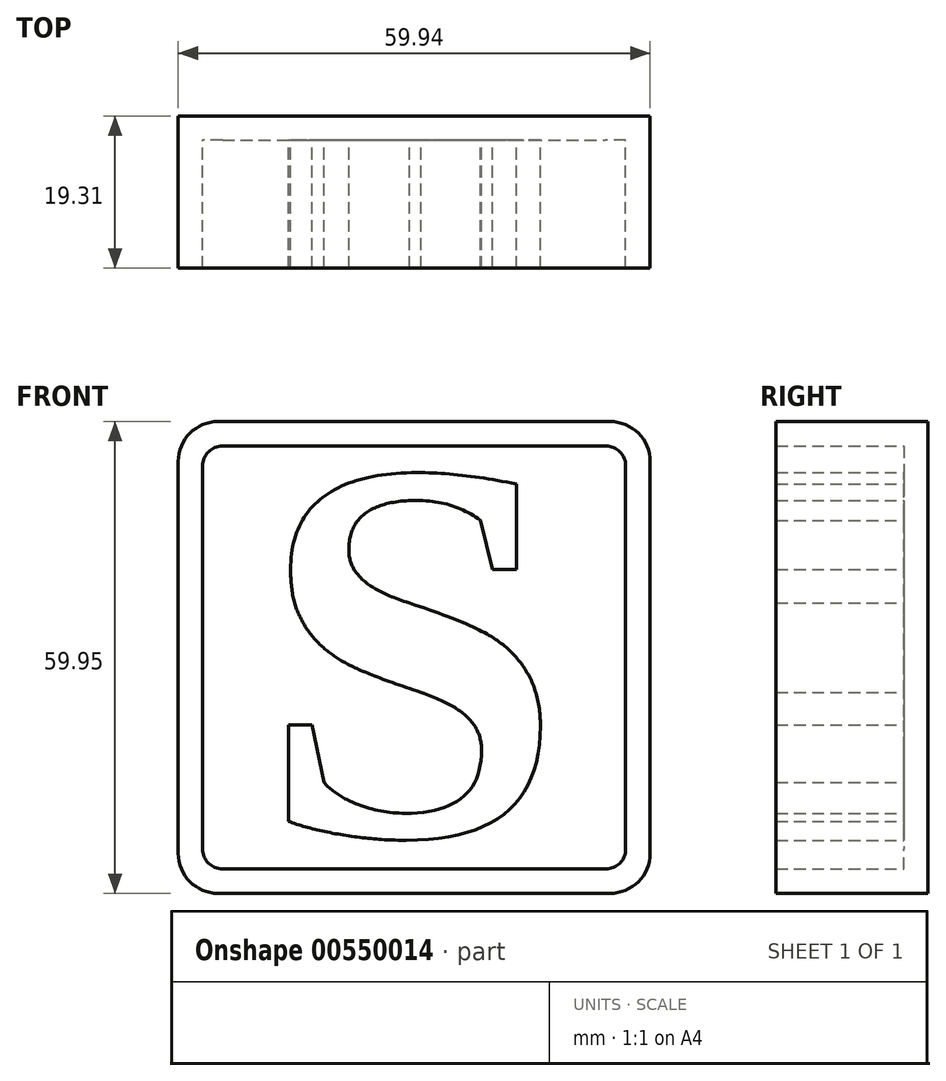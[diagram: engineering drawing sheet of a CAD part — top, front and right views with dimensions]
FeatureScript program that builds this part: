
annotation { "Feature Type Name" : "Feature", "Feature Type Description" : "" }
export const myFeature = defineFeature(function(context is Context, id is Id, definition is map)
    precondition{}
    {
        {
            var Q0;
            Q0=qCreatedBy(makeId("Front.planeOp"),FACE);
            var sketch = newSketch(context, id + "F0", { "sketchPlane" : qUnion([Q0])});
            skText(sketch, "E0", { "text": "S", "fontName": "Tinos-Bold.ttf"});
            const initialGuessF0  = {"E0": [-0.03634, -0.01847, 1, 0, 0.05004]};
            skSetInitialGuess(sketch, initialGuessF0);
            skSolve(sketch);
        }
        {
            var Q0;
            Q0=makeQuery(id+"F0.imprint","IMPRINT",FACE,{"disambiguationData":[TD([[makeQuery(id+"F0.imprint","IMPRINT",EDGE,{"derivedFrom":sQuery(id+"F0.wireOp",EDGE,"E0.sketch_text.stroke-0")}),-1.0]])]});
            extrude(context, id + "F1", {"entities" : qUnion([Q0]), "depth" : 9.9 * mm, "offsetDistance" : 25.4 * mm});
        }
        {
            var Q0;
            Q0=makeQuery(id+"F1.opExtrude","CAP_FACE",FACE,{"disambiguationData":[OSD([sQuery(id+"F0.wireOp",EDGE,"E0.sketch_text.stroke-0"),sQuery(id+"F0.wireOp",EDGE,"E0.sketch_text.stroke-1"),sQuery(id+"F0.wireOp",EDGE,"E0.sketch_text.stroke-2"),sQuery(id+"F0.wireOp",EDGE,"E0.sketch_text.stroke-3"),sQuery(id+"F0.wireOp",EDGE,"E0.sketch_text.stroke-4"),sQuery(id+"F0.wireOp",EDGE,"E0.sketch_text.stroke-5"),sQuery(id+"F0.wireOp",EDGE,"E0.sketch_text.stroke-6"),sQuery(id+"F0.wireOp",EDGE,"E0.sketch_text.stroke-7"),sQuery(id+"F0.wireOp",EDGE,"E0.sketch_text.stroke-8"),sQuery(id+"F0.wireOp",EDGE,"E0.sketch_text.stroke-9"),sQuery(id+"F0.wireOp",EDGE,"E0.sketch_text.stroke-10"),sQuery(id+"F0.wireOp",EDGE,"E0.sketch_text.stroke-11"),sQuery(id+"F0.wireOp",EDGE,"E0.sketch_text.stroke-12"),sQuery(id+"F0.wireOp",EDGE,"E0.sketch_text.stroke-13"),sQuery(id+"F0.wireOp",EDGE,"E0.sketch_text.stroke-14"),sQuery(id+"F0.wireOp",EDGE,"E0.sketch_text.stroke-15"),sQuery(id+"F0.wireOp",EDGE,"E0.sketch_text.stroke-16"),sQuery(id+"F0.wireOp",EDGE,"E0.sketch_text.stroke-17"),sQuery(id+"F0.wireOp",EDGE,"E0.sketch_text.stroke-18"),sQuery(id+"F0.wireOp",EDGE,"E0.sketch_text.stroke-19"),sQuery(id+"F0.wireOp",EDGE,"E0.sketch_text.stroke-20"),sQuery(id+"F0.wireOp",EDGE,"E0.sketch_text.stroke-21"),sQuery(id+"F0.wireOp",EDGE,"E0.sketch_text.stroke-22"),sQuery(id+"F0.wireOp",EDGE,"E0.sketch_text.stroke-23"),sQuery(id+"F0.wireOp",EDGE,"E0.sketch_text.stroke-24"),sQuery(id+"F0.wireOp",EDGE,"E0.sketch_text.stroke-25"),sQuery(id+"F0.wireOp",EDGE,"E0.sketch_text.stroke-26"),sQuery(id+"F0.wireOp",EDGE,"E0.sketch_text.stroke-27"),sQuery(id+"F0.wireOp",EDGE,"E0.sketch_text.stroke-28")])],"isStart":true});
            var sketch = newSketch(context, id + "F2", { "sketchPlane" : qUnion([Q0])});
            skLineSegment(sketch, "E1.bottom", {"start": v(-13.3, 34.04) * mm, "end": v(46.64, 34.04) * mm});
            skLineSegment(sketch, "E1.top", {"start": v(-13.3, -25.9) * mm, "end": v(46.64, -25.9) * mm});
            skLineSegment(sketch, "E1.left", {"start": v(-13.3, 34.04) * mm, "end": v(-13.3, -25.9) * mm});
            skLineSegment(sketch, "E1.right", {"start": v(46.64, 34.04) * mm, "end": v(46.64, -25.9) * mm});
            skSolve(sketch);
        }
        {
            var Q0;
            Q0=makeQuery(id+"F2.imprint","IMPRINT",FACE,{"disambiguationData":[TD([[makeQuery(id+"F2.imprint","IMPRINT",EDGE,{"derivedFrom":sQuery(id+"F2.wireOp",EDGE,"E1.bottom")}),-1.0]])]});
            var Q1;
            Q1=makeQuery(id+"F2.imprint","IMPRINT",FACE,{"disambiguationData":[TD([[makeQuery(id+"F2.imprint","IMPRINT",EDGE,{"derivedFrom":makeQuery(id+"F1.opExtrude","CAP_EDGE",EDGE,{"disambiguationData":[OSD([sQuery(id+"F0.wireOp",EDGE,"E0.sketch_text.stroke-0")])],"isStart":true})}),1.0]])]});
            var Q2;
            Q2=sQuery(id+"F2.wireOp",EDGE,"E1.right");
            var Q3;
            Q3=sQuery(id+"F2.wireOp",EDGE,"E1.bottom");
            var Q4;
            Q4=sQuery(id+"F2.wireOp",EDGE,"E1.top");
            var Q5;
            Q5=sQuery(id+"F2.wireOp",EDGE,"E1.left");
            extrude(context, id + "F3", {"entities" : qUnion([Q0, Q1]), "operationType" : NewBodyOperationType.ADD, "surfaceEntities" : qUnion([Q2, Q3, Q4, Q5]), "depth" : 3.05 * mm, "offsetDistance" : 25.4 * mm});
        }
        {
            var Q0;
            Q0=makeQuery(id+"F3.opExtrude","CAP_FACE",FACE,{"disambiguationData":[OSD([sQuery(id+"F2.wireOp",EDGE,"E1.bottom"),sQuery(id+"F2.wireOp",EDGE,"E1.top"),sQuery(id+"F2.wireOp",EDGE,"E1.left"),sQuery(id+"F2.wireOp",EDGE,"E1.right")])],"isStart":true});
            var sketch = newSketch(context, id + "F4", { "sketchPlane" : qUnion([Q0])});
            skLineSegment(sketch, "E2.bottom", {"start": v(-43.54, 30.94) * mm, "end": v(10.2, 30.94) * mm});
            skLineSegment(sketch, "E2.top", {"start": v(-43.54, -22.8) * mm, "end": v(10.2, -22.8) * mm});
            skLineSegment(sketch, "E2.left", {"start": v(-43.54, 30.94) * mm, "end": v(-43.54, -22.8) * mm});
            skLineSegment(sketch, "E2.right", {"start": v(10.2, 30.94) * mm, "end": v(10.2, -22.8) * mm});
            skSolve(sketch);
        }
        {
            var Q0;
            Q0=makeQuery(id+"F4.imprint","IMPRINT",FACE,{"disambiguationData":[TD([[makeQuery(id+"F4.imprint","IMPRINT",EDGE,{"derivedFrom":sQuery(id+"F4.wireOp",EDGE,"E2.bottom")}),1.0]])]});
            extrude(context, id + "F5", {"entities" : qUnion([Q0]), "operationType" : NewBodyOperationType.ADD, "depth" : 9.9 * mm, "offsetDistance" : 25.4 * mm});
        }
        {
            var Q0;
            {var subQ0=sQuery(id+"F2.wireOp",EDGE,"E1.left");var subQ1=sQuery(id+"F2.wireOp",EDGE,"E1.bottom");Q0=makeQuery(id+"F5.boolean.opBoolean","MERGE",EDGE,{"derivedFrom":[makeQuery(id+"F3.opExtrude","SWEPT_EDGE",EDGE,{"disambiguationData":[OSD([subQ1,subQ0])]}),makeQuery(id+"F5.opExtrude","SWEPT_EDGE",EDGE,{"disambiguationData":[OSD([subQ1,subQ0])]})]});}
            var Q1;
            {var subQ0=sQuery(id+"F2.wireOp",EDGE,"E1.right");var subQ1=sQuery(id+"F2.wireOp",EDGE,"E1.bottom");Q1=makeQuery(id+"F5.boolean.opBoolean","MERGE",EDGE,{"derivedFrom":[makeQuery(id+"F3.opExtrude","SWEPT_EDGE",EDGE,{"disambiguationData":[OSD([subQ1,subQ0])]}),makeQuery(id+"F5.opExtrude","SWEPT_EDGE",EDGE,{"disambiguationData":[OSD([subQ1,subQ0])]})]});}
            var Q2;
            {var subQ0=sQuery(id+"F2.wireOp",EDGE,"E1.right");var subQ1=sQuery(id+"F2.wireOp",EDGE,"E1.top");Q2=makeQuery(id+"F5.boolean.opBoolean","MERGE",EDGE,{"derivedFrom":[makeQuery(id+"F3.opExtrude","SWEPT_EDGE",EDGE,{"disambiguationData":[OSD([subQ1,subQ0])]}),makeQuery(id+"F5.opExtrude","SWEPT_EDGE",EDGE,{"disambiguationData":[OSD([subQ1,subQ0])]})]});}
            var Q3;
            {var subQ0=sQuery(id+"F2.wireOp",EDGE,"E1.left");var subQ1=sQuery(id+"F2.wireOp",EDGE,"E1.top");Q3=makeQuery(id+"F5.boolean.opBoolean","MERGE",EDGE,{"derivedFrom":[makeQuery(id+"F3.opExtrude","SWEPT_EDGE",EDGE,{"disambiguationData":[OSD([subQ1,subQ0])]}),makeQuery(id+"F5.opExtrude","SWEPT_EDGE",EDGE,{"disambiguationData":[OSD([subQ1,subQ0])]})]});}
            fillet(context, id + "F6", {"entities" : qUnion([Q0, Q1, Q2, Q3]), "radius" : 5.08 * mm, "tangentPropagation" : true, "allowEdgeOverflow" : false});
        }
        {
            var Q0;
            Q0=makeQuery(id+"F5.opExtrude","SWEPT_EDGE",EDGE,{"disambiguationData":[OSD([sQuery(id+"F4.wireOp",EDGE,"E2.bottom"),sQuery(id+"F4.wireOp",EDGE,"E2.left")])]});
            var Q1;
            Q1=makeQuery(id+"F5.opExtrude","SWEPT_EDGE",EDGE,{"disambiguationData":[OSD([sQuery(id+"F4.wireOp",EDGE,"E2.bottom"),sQuery(id+"F4.wireOp",EDGE,"E2.right")])]});
            var Q2;
            Q2=makeQuery(id+"F5.opExtrude","SWEPT_EDGE",EDGE,{"disambiguationData":[OSD([sQuery(id+"F4.wireOp",EDGE,"E2.top"),sQuery(id+"F4.wireOp",EDGE,"E2.right")])]});
            var Q3;
            Q3=makeQuery(id+"F5.opExtrude","SWEPT_EDGE",EDGE,{"disambiguationData":[OSD([sQuery(id+"F4.wireOp",EDGE,"E2.top"),sQuery(id+"F4.wireOp",EDGE,"E2.left")])]});
            fillet(context, id + "F7", {"entities" : qUnion([Q0, Q1, Q2, Q3]), "radius" : 2.54 * mm, "tangentPropagation" : true, "allowEdgeOverflow" : false});
        }
        {
            var Q0;
            Q0=makeQuery(id+"F1.opExtrude","CAP_FACE",FACE,{"disambiguationData":[OSD([sQuery(id+"F0.wireOp",EDGE,"E0.sketch_text.stroke-0"),sQuery(id+"F0.wireOp",EDGE,"E0.sketch_text.stroke-1"),sQuery(id+"F0.wireOp",EDGE,"E0.sketch_text.stroke-2"),sQuery(id+"F0.wireOp",EDGE,"E0.sketch_text.stroke-3"),sQuery(id+"F0.wireOp",EDGE,"E0.sketch_text.stroke-4"),sQuery(id+"F0.wireOp",EDGE,"E0.sketch_text.stroke-5"),sQuery(id+"F0.wireOp",EDGE,"E0.sketch_text.stroke-6"),sQuery(id+"F0.wireOp",EDGE,"E0.sketch_text.stroke-7"),sQuery(id+"F0.wireOp",EDGE,"E0.sketch_text.stroke-8"),sQuery(id+"F0.wireOp",EDGE,"E0.sketch_text.stroke-9"),sQuery(id+"F0.wireOp",EDGE,"E0.sketch_text.stroke-10"),sQuery(id+"F0.wireOp",EDGE,"E0.sketch_text.stroke-11"),sQuery(id+"F0.wireOp",EDGE,"E0.sketch_text.stroke-12"),sQuery(id+"F0.wireOp",EDGE,"E0.sketch_text.stroke-13"),sQuery(id+"F0.wireOp",EDGE,"E0.sketch_text.stroke-14"),sQuery(id+"F0.wireOp",EDGE,"E0.sketch_text.stroke-15"),sQuery(id+"F0.wireOp",EDGE,"E0.sketch_text.stroke-16"),sQuery(id+"F0.wireOp",EDGE,"E0.sketch_text.stroke-17"),sQuery(id+"F0.wireOp",EDGE,"E0.sketch_text.stroke-18"),sQuery(id+"F0.wireOp",EDGE,"E0.sketch_text.stroke-19"),sQuery(id+"F0.wireOp",EDGE,"E0.sketch_text.stroke-20"),sQuery(id+"F0.wireOp",EDGE,"E0.sketch_text.stroke-21"),sQuery(id+"F0.wireOp",EDGE,"E0.sketch_text.stroke-22"),sQuery(id+"F0.wireOp",EDGE,"E0.sketch_text.stroke-23"),sQuery(id+"F0.wireOp",EDGE,"E0.sketch_text.stroke-24"),sQuery(id+"F0.wireOp",EDGE,"E0.sketch_text.stroke-25"),sQuery(id+"F0.wireOp",EDGE,"E0.sketch_text.stroke-26"),sQuery(id+"F0.wireOp",EDGE,"E0.sketch_text.stroke-27"),sQuery(id+"F0.wireOp",EDGE,"E0.sketch_text.stroke-28")])],"isStart":false});
            var Q1;
            Q1=makeQuery(id+"F5.opExtrude","CAP_FACE",FACE,{"disambiguationData":[OSD([sQuery(id+"F2.wireOp",EDGE,"E1.bottom"),sQuery(id+"F2.wireOp",EDGE,"E1.top"),sQuery(id+"F2.wireOp",EDGE,"E1.left"),sQuery(id+"F2.wireOp",EDGE,"E1.right"),sQuery(id+"F4.wireOp",EDGE,"E2.bottom"),sQuery(id+"F4.wireOp",EDGE,"E2.top"),sQuery(id+"F4.wireOp",EDGE,"E2.left"),sQuery(id+"F4.wireOp",EDGE,"E2.right")])],"isStart":false});
            extrude(context, id + "F8", {"entities" : qUnion([Q0, Q1]), "operationType" : NewBodyOperationType.ADD, "depth" : 6.35 * mm, "offsetDistance" : 25.4 * mm});
        }
    });
